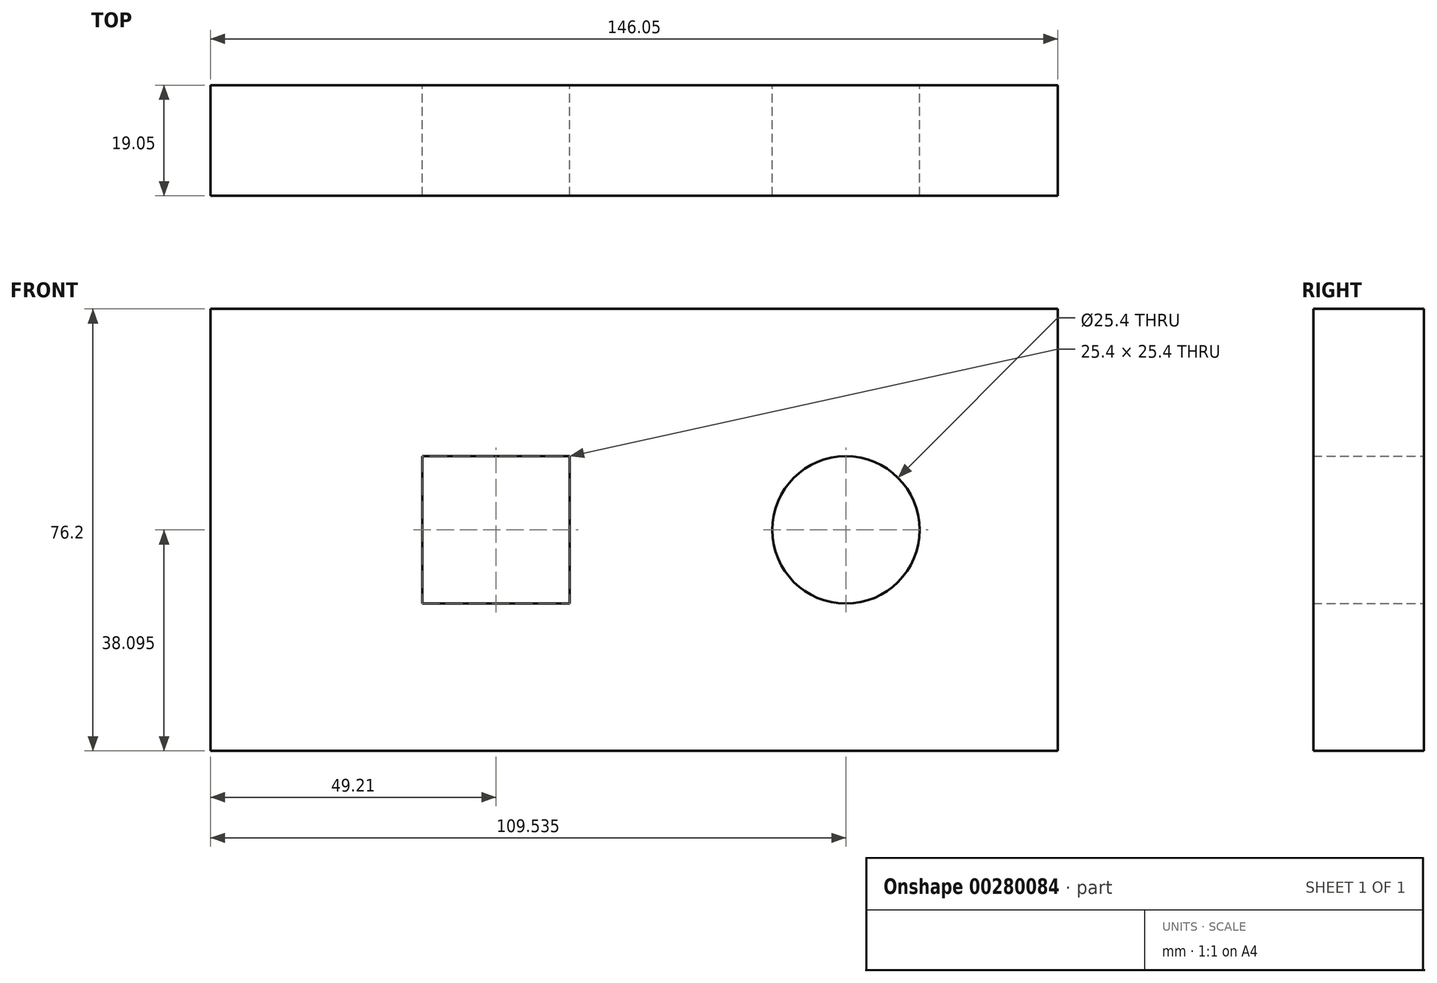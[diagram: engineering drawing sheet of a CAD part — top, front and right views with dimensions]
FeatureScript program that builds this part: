
annotation { "Feature Type Name" : "Feature", "Feature Type Description" : "" }
export const myFeature = defineFeature(function(context is Context, id is Id, definition is map)
    precondition{}
    {
        {
            var Q0;
            Q0=qCreatedBy(makeId("Front.planeOp"),FACE);
            var sketch = newSketch(context, id + "F0", { "sketchPlane" : qUnion([Q0])});
            skLineSegment(sketch, "E0.bottom", {"start": v(-55.66, -14.87) * mm, "end": v(90.39, -14.87) * mm});
            skLineSegment(sketch, "E0.top", {"start": v(-55.66, 61.33) * mm, "end": v(90.39, 61.33) * mm});
            skLineSegment(sketch, "E0.left", {"start": v(-55.66, -14.87) * mm, "end": v(-55.66, 61.33) * mm});
            skLineSegment(sketch, "E0.right", {"start": v(90.39, -14.87) * mm, "end": v(90.39, 61.33) * mm});
            skCircle(sketch, "E1", {"center": v(53.88, 23.23) * mm, "radius": 12.7 * mm});
            skLineSegment(sketch, "E2.bottom", {"start": v(-19.15, 35.93) * mm, "end": v(6.25, 35.93) * mm});
            skLineSegment(sketch, "E2.top", {"start": v(-19.15, 10.53) * mm, "end": v(6.25, 10.53) * mm});
            skLineSegment(sketch, "E2.left", {"start": v(-19.15, 35.93) * mm, "end": v(-19.15, 10.53) * mm});
            skLineSegment(sketch, "E2.right", {"start": v(6.25, 35.93) * mm, "end": v(6.25, 10.53) * mm});
            skSolve(sketch);
        }
        {
            var Q0;
            Q0 = qSketchRegion(id + "F0", true);
            extrude(context, id + "F1", {"entities" : qUnion([Q0]), "depth" : 19.05 * mm});
        }
    });
